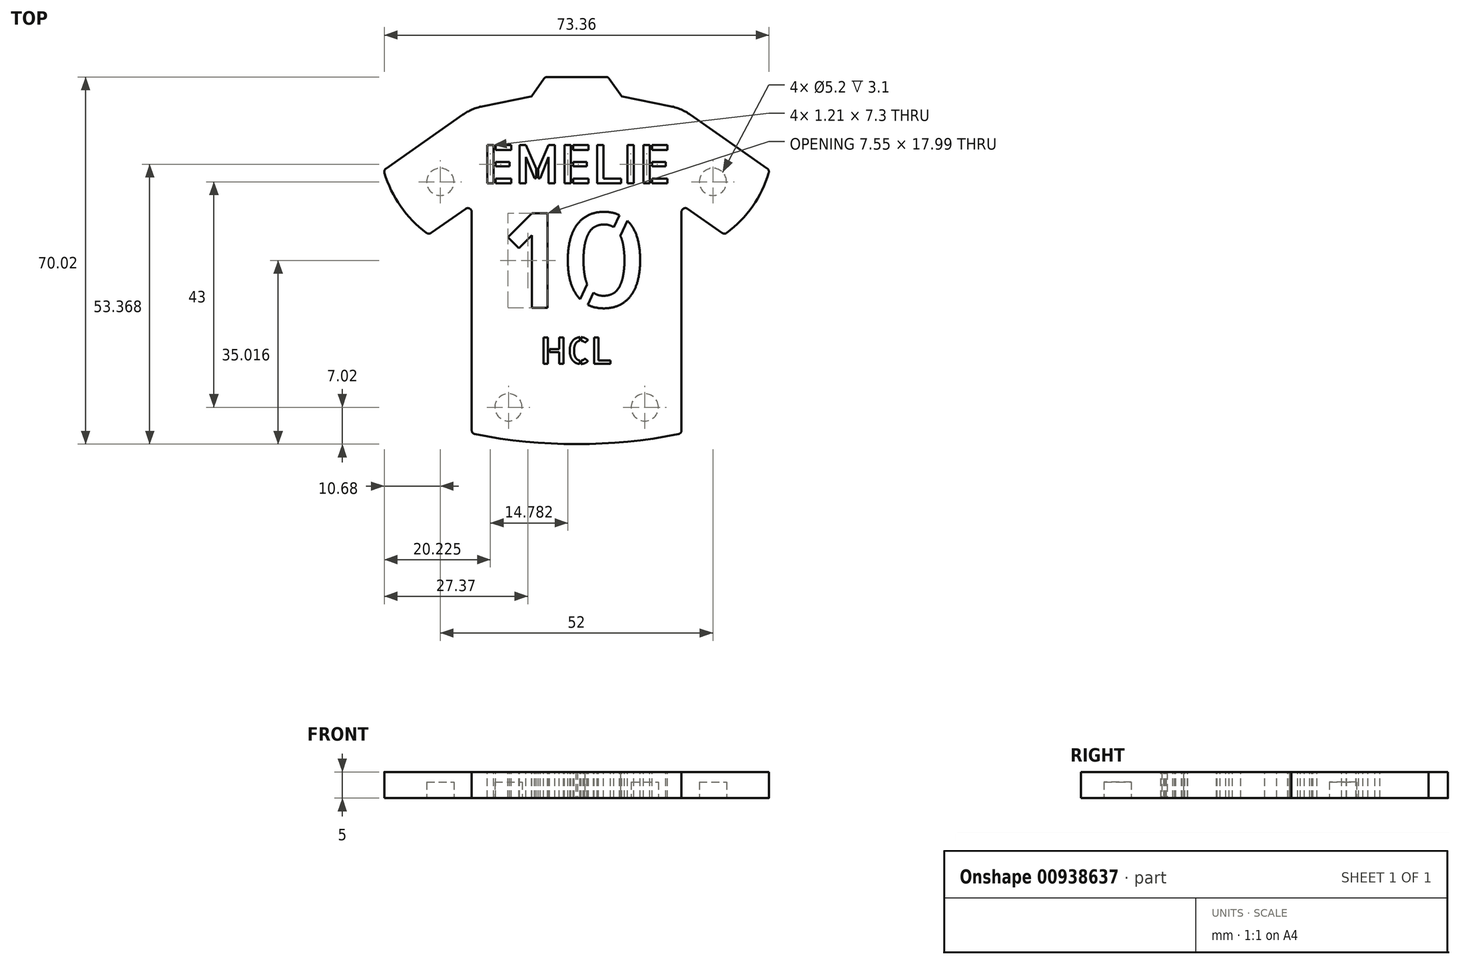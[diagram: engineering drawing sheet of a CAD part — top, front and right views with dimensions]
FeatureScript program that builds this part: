
annotation { "Feature Type Name" : "Feature", "Feature Type Description" : "" }
export const myFeature = defineFeature(function(context is Context, id is Id, definition is map)
    precondition{}
    {
        {
            var Q0;
            Q0=qCreatedBy(makeId("Top.planeOp"),FACE);
            var sketch = newSketch(context, id + "F0", { "sketchPlane" : qUnion([Q0])});
            skLineSegment(sketch, "E0", {"start": v(0, 0) * mm, "end": v(0, -62) * mm, "construction": true});
            skLineSegment(sketch, "E1", {"start": v(0, -62) * mm, "end": v(-20, -62) * mm, "construction": true});
            skLineSegment(sketch, "E2", {"start": v(-20, -62) * mm, "end": v(-20, -18.31) * mm});
            skLineSegment(sketch, "E3", {"start": v(-20, -18.31) * mm, "end": v(-28.2, -24.05) * mm});
            skLineSegment(sketch, "E4", {"start": v(-28.2, -24.05) * mm, "end": v(-36.8, -11.76) * mm, "construction": true});
            skLineSegment(sketch, "E5", {"start": v(-36.8, -11.76) * mm, "end": v(-20, 0) * mm});
            skLineSegment(sketch, "E6.MirrorCS", {"start": v(36.8, -11.76) * mm, "end": v(20, 0) * mm});
            skLineSegment(sketch, "E7.MirrorCS", {"start": v(28.2, -24.05) * mm, "end": v(36.8, -11.76) * mm, "construction": true});
            skLineSegment(sketch, "E8.MirrorCS", {"start": v(20, -62) * mm, "end": v(20, -18.31) * mm});
            skLineSegment(sketch, "E9.MirrorCS", {"start": v(0, -62) * mm, "end": v(20, -62) * mm, "construction": true});
            skLineSegment(sketch, "E10.MirrorCS", {"start": v(20, -18.31) * mm, "end": v(28.2, -24.05) * mm});
            skPoint(sketch, "E11.orphan", {"position": v(0, 0) * mm});
            skLineSegment(sketch, "E12", {"start": v(-20, 0) * mm, "end": v(0, 4) * mm});
            skLineSegment(sketch, "E13", {"start": v(20, 0) * mm, "end": v(0, 4) * mm});
            skArc(sketch, "E14", {"start": v(-36.8, -11.76) * mm, "mid": v(-33.57, -18.66) * mm, "end": v(-28.2, -24.05) * mm});
            skArc(sketch, "E15", {"start": v(28.2, -24.05) * mm, "mid": v(33.57, -18.66) * mm, "end": v(36.8, -11.76) * mm});
            skArc(sketch, "E16", {"start": v(-20, -62) * mm, "mid": v(0, -64.02) * mm, "end": v(20, -62) * mm});
            skSolve(sketch);
        }
        {
            var Q0;
            Q0=qSketchRegion(id+"F0",true);
            extrude(context, id + "F1", {"entities" : qUnion([Q0]), "depth" : 5 * mm, "offsetDistance" : 25 * mm});
        }
        {
            var Q0;
            Q0=makeQuery(id+"F1.opExtrude","CAP_FACE",FACE,{"disambiguationData":[OSD([sQuery(id+"F0.wireOp",EDGE,"E1"),sQuery(id+"F0.wireOp",EDGE,"E2"),sQuery(id+"F0.wireOp",EDGE,"E3"),sQuery(id+"F0.wireOp",EDGE,"E4"),sQuery(id+"F0.wireOp",EDGE,"E5"),sQuery(id+"F0.wireOp",EDGE,"IlW5oEZI-P582-iyz9-SPjp-bK7lNdtFADA4"),sQuery(id+"F0.wireOp",EDGE,"b0af1ca9-168d-4077-b48c-e6805785c7b00.MirrorCS"),sQuery(id+"F0.wireOp",EDGE,"E6.MirrorCS"),sQuery(id+"F0.wireOp",EDGE,"E7.MirrorCS"),sQuery(id+"F0.wireOp",EDGE,"E8.MirrorCS"),sQuery(id+"F0.wireOp",EDGE,"E9.MirrorCS"),sQuery(id+"F0.wireOp",EDGE,"E10.MirrorCS")])],"isStart":true});
            var Q1;
            Q1=makeQuery(id+"F1.opExtrude","CAP_FACE",FACE,{"disambiguationData":[OSD([sQuery(id+"F0.wireOp",EDGE,"E1"),sQuery(id+"F0.wireOp",EDGE,"E2"),sQuery(id+"F0.wireOp",EDGE,"E3"),sQuery(id+"F0.wireOp",EDGE,"E4"),sQuery(id+"F0.wireOp",EDGE,"E5"),sQuery(id+"F0.wireOp",EDGE,"E6.MirrorCS"),sQuery(id+"F0.wireOp",EDGE,"E7.MirrorCS"),sQuery(id+"F0.wireOp",EDGE,"E8.MirrorCS"),sQuery(id+"F0.wireOp",EDGE,"E9.MirrorCS"),sQuery(id+"F0.wireOp",EDGE,"E10.MirrorCS"),sQuery(id+"F0.wireOp",EDGE,"E12"),sQuery(id+"F0.wireOp",EDGE,"E13")])],"isStart":false});
            var sketch = newSketch(context, id + "F2", { "sketchPlane" : qUnion([Q0, Q1])});
            skCircle(sketch, "E17", {"center": v(13, 57) * mm, "radius": 2.6 * mm});
            skCircle(sketch, "E18", {"center": v(-13, 57) * mm, "radius": 2.6 * mm});
            skCircle(sketch, "E19", {"center": v(26, 14) * mm, "radius": 2.6 * mm});
            skCircle(sketch, "E20", {"center": v(-26, 14) * mm, "radius": 2.6 * mm});
            skSolve(sketch);
        }
        {
            var Q0;
            Q0=qSketchRegion(id+"F2",true);
            extrude(context, id + "F3", {"entities" : qUnion([Q0]), "operationType" : NewBodyOperationType.REMOVE, "oppositeDirection" : true, "depth" : 3.1 * mm, "offsetDistance" : 25 * mm});
        }
        {
            var Q0;
            Q0=makeQuery(id+"F1.opExtrude","CAP_FACE",FACE,{"disambiguationData":[OSD([sQuery(id+"F0.wireOp",EDGE,"E1"),sQuery(id+"F0.wireOp",EDGE,"E2"),sQuery(id+"F0.wireOp",EDGE,"E3"),sQuery(id+"F0.wireOp",EDGE,"E4"),sQuery(id+"F0.wireOp",EDGE,"E5"),sQuery(id+"F0.wireOp",EDGE,"IlW5oEZI-P582-iyz9-SPjp-bK7lNdtFADA4"),sQuery(id+"F0.wireOp",EDGE,"b0af1ca9-168d-4077-b48c-e6805785c7b00.MirrorCS"),sQuery(id+"F0.wireOp",EDGE,"E6.MirrorCS"),sQuery(id+"F0.wireOp",EDGE,"E7.MirrorCS"),sQuery(id+"F0.wireOp",EDGE,"E8.MirrorCS"),sQuery(id+"F0.wireOp",EDGE,"E9.MirrorCS"),sQuery(id+"F0.wireOp",EDGE,"E10.MirrorCS"),sQuery(id+"F0.wireOp",EDGE,"k2Sst70w-Y1rZ-SRoK-z35Y-7HSdN3ftnpVl")])],"isStart":false});
            var sketch = newSketch(context, id + "F4", { "sketchPlane" : qUnion([Q0])});
            skText(sketch, "E21", { "text": "EMELIE", "fontName": "AllertaStencil-Regular.ttf"});
            skText(sketch, "E22", { "text": "10", "fontName": "AllertaStencil-Regular.ttf"});
            skText(sketch, "E23", { "text": "HCL", "fontName": "AllertaStencil-Regular.ttf"});
            const initialGuessF4  = {"E21": [-0.018, -0.0143, 1, 0, 0.0073], "E22": [-0.01379, -0.038, 1, 0, 0.018], "E23": [-0.00693, -0.0487, 1, 0, 0.005]};
            skSetInitialGuess(sketch, initialGuessF4);
            skSolve(sketch);
        }
        {
            var Q0;
            Q0=qSketchRegion(id+"F4",true);
            extrude(context, id + "F5", {"entities" : qUnion([Q0]), "operationType" : NewBodyOperationType.REMOVE, "endBound" : BoundingType.THROUGH_ALL, "oppositeDirection" : true, "depth" : 25 * mm, "offsetDistance" : 25 * mm});
        }
        {
            var Q0;
            Q0=makeQuery(id+"F1.opExtrude","CAP_FACE",FACE,{"disambiguationData":[OSD([sQuery(id+"F0.wireOp",EDGE,"E1"),sQuery(id+"F0.wireOp",EDGE,"E2"),sQuery(id+"F0.wireOp",EDGE,"E3"),sQuery(id+"F0.wireOp",EDGE,"E4"),sQuery(id+"F0.wireOp",EDGE,"E5"),sQuery(id+"F0.wireOp",EDGE,"E6.MirrorCS"),sQuery(id+"F0.wireOp",EDGE,"E7.MirrorCS"),sQuery(id+"F0.wireOp",EDGE,"E8.MirrorCS"),sQuery(id+"F0.wireOp",EDGE,"E9.MirrorCS"),sQuery(id+"F0.wireOp",EDGE,"E10.MirrorCS"),sQuery(id+"F0.wireOp",EDGE,"E12"),sQuery(id+"F0.wireOp",EDGE,"E13")])],"isStart":false});
            var sketch = newSketch(context, id + "F6", { "sketchPlane" : qUnion([Q0])});
            skLineSegment(sketch, "E24", {"start": v(-8.6, 2.28) * mm, "end": v(-6, 6) * mm});
            skLineSegment(sketch, "E25", {"start": v(-6, 6) * mm, "end": v(6, 6) * mm});
            skLineSegment(sketch, "E26", {"start": v(6, 6) * mm, "end": v(8.6, 2.28) * mm});
            skLineSegment(sketch, "E27", {"start": v(-8.6, 2.28) * mm, "end": v(0, 4) * mm});
            skLineSegment(sketch, "E28", {"start": v(0, 4) * mm, "end": v(8.6, 2.28) * mm});
            skSolve(sketch);
        }
        {
            var Q0;
            Q0=qSketchRegion(id+"F6",true);
            extrude(context, id + "F7", {"entities" : qUnion([Q0]), "operationType" : NewBodyOperationType.ADD, "oppositeDirection" : true, "depth" : 5 * mm, "offsetDistance" : 25 * mm});
        }
        {
            var Q0;
            Q0=makeQuery(id+"F1.opExtrude","SWEPT_EDGE",EDGE,{"disambiguationData":[OSD([sQuery(id+"F0.wireOp",EDGE,"E5"),sQuery(id+"F0.wireOp",EDGE,"E12")])]});
            var Q1;
            Q1=makeQuery(id+"F1.opExtrude","SWEPT_EDGE",EDGE,{"disambiguationData":[OSD([sQuery(id+"F0.wireOp",EDGE,"E6.MirrorCS"),sQuery(id+"F0.wireOp",EDGE,"E13")])]});
            fillet(context, id + "F8", {"entities" : qUnion([Q0, Q1]), "radius" : 10 * mm, "tangentPropagation" : true, "allowEdgeOverflow" : false});
        }
        {
            var Q0;
            Q0=makeQuery(id+"F7.opExtrude","SWEPT_EDGE",EDGE,{"disambiguationData":[OSD([sQuery(id+"F6.wireOp",EDGE,"E24"),sQuery(id+"F6.wireOp",EDGE,"E25")])]});
            var Q1;
            Q1=makeQuery(id+"F7.opExtrude","SWEPT_EDGE",EDGE,{"disambiguationData":[OSD([sQuery(id+"F6.wireOp",EDGE,"E25"),sQuery(id+"F6.wireOp",EDGE,"E26")])]});
            var Q2;
            Q2=makeQuery(id+"F7.opExtrude","SWEPT_EDGE",EDGE,{"disambiguationData":[OSD([sQuery(id+"F0.wireOp",EDGE,"E12"),sQuery(id+"F6.wireOp",EDGE,"E24"),sQuery(id+"F6.wireOp",EDGE,"E27")])]});
            var Q3;
            Q3=makeQuery(id+"F1.opExtrude","SWEPT_EDGE",EDGE,{"disambiguationData":[OSD([sQuery(id+"F0.wireOp",EDGE,"E5"),sQuery(id+"F0.wireOp",EDGE,"E14")])]});
            var Q4;
            Q4=makeQuery(id+"F1.opExtrude","SWEPT_EDGE",EDGE,{"disambiguationData":[OSD([sQuery(id+"F0.wireOp",EDGE,"E6.MirrorCS"),sQuery(id+"F0.wireOp",EDGE,"E15")])]});
            var Q5;
            Q5=makeQuery(id+"F1.opExtrude","SWEPT_EDGE",EDGE,{"disambiguationData":[OSD([sQuery(id+"F0.wireOp",EDGE,"E10.MirrorCS"),sQuery(id+"F0.wireOp",EDGE,"E15")])]});
            var Q6;
            Q6=makeQuery(id+"F1.opExtrude","SWEPT_EDGE",EDGE,{"disambiguationData":[OSD([sQuery(id+"F0.wireOp",EDGE,"E8.MirrorCS"),sQuery(id+"F0.wireOp",EDGE,"E10.MirrorCS")])]});
            var Q7;
            Q7=makeQuery(id+"F1.opExtrude","SWEPT_EDGE",EDGE,{"disambiguationData":[OSD([sQuery(id+"F0.wireOp",EDGE,"E2"),sQuery(id+"F0.wireOp",EDGE,"E3")])]});
            var Q8;
            Q8=makeQuery(id+"F1.opExtrude","SWEPT_EDGE",EDGE,{"disambiguationData":[OSD([sQuery(id+"F0.wireOp",EDGE,"E2"),sQuery(id+"F0.wireOp",EDGE,"E16")])]});
            var Q9;
            Q9=makeQuery(id+"F1.opExtrude","SWEPT_EDGE",EDGE,{"disambiguationData":[OSD([sQuery(id+"F0.wireOp",EDGE,"E8.MirrorCS"),sQuery(id+"F0.wireOp",EDGE,"E16")])]});
            var Q10;
            Q10=makeQuery(id+"F1.opExtrude","SWEPT_EDGE",EDGE,{"disambiguationData":[OSD([sQuery(id+"F0.wireOp",EDGE,"E3"),sQuery(id+"F0.wireOp",EDGE,"E14")])]});
            var Q11;
            Q11=makeQuery(id+"F7.opExtrude","SWEPT_EDGE",EDGE,{"disambiguationData":[OSD([sQuery(id+"F0.wireOp",EDGE,"E13"),sQuery(id+"F6.wireOp",EDGE,"E26"),sQuery(id+"F6.wireOp",EDGE,"E28")])]});
            fillet(context, id + "F9", {"entities" : qUnion([Q0, Q1, Q2, Q3, Q4, Q5, Q6, Q7, Q8, Q9, Q10, Q11]), "radius" : 0.75 * mm, "tangentPropagation" : true, "allowEdgeOverflow" : false});
        }
    });
